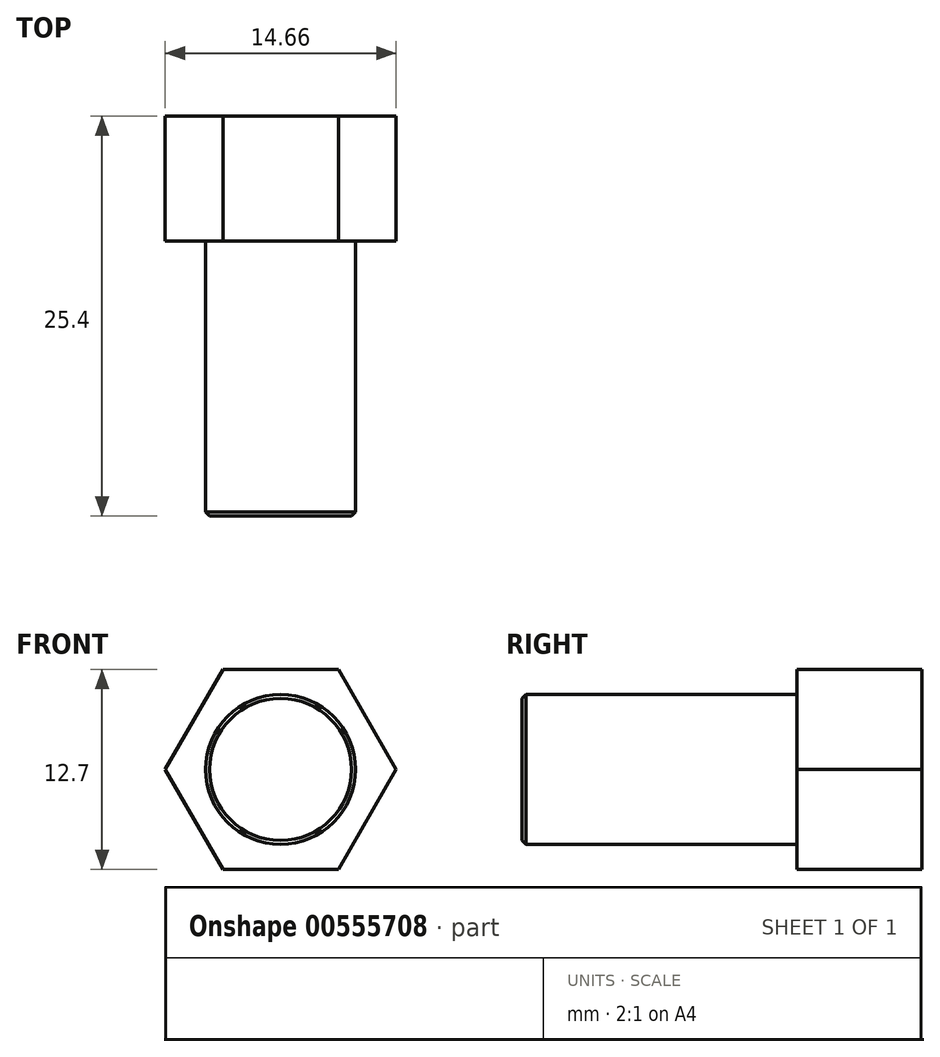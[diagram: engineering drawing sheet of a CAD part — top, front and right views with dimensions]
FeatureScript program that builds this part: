
annotation { "Feature Type Name" : "Feature", "Feature Type Description" : "" }
export const myFeature = defineFeature(function(context is Context, id is Id, definition is map)
    precondition{}
    {
        {
            var Q0;
            Q0=qCreatedBy(makeId("Front.planeOp"),FACE);
            var sketch = newSketch(context, id + "F0", { "sketchPlane" : qUnion([Q0])});
            skCircle(sketch, "E0", {"center": v(0, 0) * mm, "radius": 4.76 * mm});
            skSolve(sketch);
        }
        {
            var Q0;
            Q0=makeQuery(id+"F0.imprint","IMPRINT",FACE,{"disambiguationData":[TD([[makeQuery(id+"F0.imprint","IMPRINT",EDGE,{"derivedFrom":sQuery(id+"F0.wireOp",EDGE,"E0")}),1.0]])]});
            extrude(context, id + "F1", {"entities" : qUnion([Q0]), "depth" : 25.4 * mm, "offsetDistance" : 25.4 * mm});
        }
        {
            var Q0;
            Q0=qCreatedBy(makeId("Front.planeOp"),FACE);
            var sketch = newSketch(context, id + "F2", { "sketchPlane" : qUnion([Q0])});
            skCircle(sketch, "E1", {"center": v(0, 0) * mm, "radius": 6.35 * mm});
            skLineSegment(sketch, "E2", {"start": v(-3.67, 6.35) * mm, "end": v(3.67, 6.35) * mm});
            skLineSegment(sketch, "E3", {"start": v(3.67, 6.35) * mm, "end": v(7.33, 0) * mm});
            skLineSegment(sketch, "E4", {"start": v(7.33, 0) * mm, "end": v(3.67, -6.35) * mm});
            skLineSegment(sketch, "E5", {"start": v(3.67, -6.35) * mm, "end": v(-3.67, -6.35) * mm});
            skLineSegment(sketch, "E6", {"start": v(-3.67, -6.35) * mm, "end": v(-7.33, 0) * mm});
            skLineSegment(sketch, "E7", {"start": v(-7.33, 0) * mm, "end": v(-3.67, 6.35) * mm});
            skSolve(sketch);
        }
        {
            var Q0;
            {var subQ0=sQuery(id+"F2.wireOp",EDGE,"E2");var subQ1=sQuery(id+"F2.wireOp",EDGE,"E1");var subQ2=makeQuery(id+"F2.imprint","INTERSECT",VERTEX,{"derivedFrom":[subQ1,subQ0]});Q0=makeQuery(id+"F2.imprint","IMPRINT",FACE,{"disambiguationData":[TD([[makeQuery(id+"F2.imprint","IMPRINT",EDGE,{"disambiguationData":[TD([[subQ2,-1.0]])],"derivedFrom":subQ1}),-1.0]])]});}
            var Q1;
            {var subQ0=sQuery(id+"F2.wireOp",EDGE,"E7");var subQ1=sQuery(id+"F2.wireOp",EDGE,"E1");var subQ2=makeQuery(id+"F2.imprint","INTERSECT",VERTEX,{"derivedFrom":[subQ1,subQ0]});Q1=makeQuery(id+"F2.imprint","IMPRINT",FACE,{"disambiguationData":[TD([[makeQuery(id+"F2.imprint","IMPRINT",EDGE,{"disambiguationData":[TD([[subQ2,-1.0]])],"derivedFrom":subQ1}),-1.0]])]});}
            var Q2;
            {var subQ0=sQuery(id+"F2.wireOp",EDGE,"E6");var subQ1=sQuery(id+"F2.wireOp",EDGE,"E1");var subQ2=makeQuery(id+"F2.imprint","INTERSECT",VERTEX,{"derivedFrom":[subQ1,subQ0]});Q2=makeQuery(id+"F2.imprint","IMPRINT",FACE,{"disambiguationData":[TD([[makeQuery(id+"F2.imprint","IMPRINT",EDGE,{"disambiguationData":[TD([[subQ2,-1.0]])],"derivedFrom":subQ1}),-1.0]])]});}
            var Q3;
            {var subQ0=sQuery(id+"F2.wireOp",EDGE,"E2");var subQ1=sQuery(id+"F2.wireOp",EDGE,"E1");var subQ2=makeQuery(id+"F2.imprint","INTERSECT",VERTEX,{"derivedFrom":[subQ1,subQ0]});Q3=makeQuery(id+"F2.imprint","IMPRINT",FACE,{"disambiguationData":[TD([[makeQuery(id+"F2.imprint","IMPRINT",EDGE,{"disambiguationData":[TD([[subQ2,1.0]])],"derivedFrom":subQ1}),-1.0]])]});}
            var Q4;
            {var subQ0=sQuery(id+"F2.wireOp",EDGE,"E3");var subQ1=sQuery(id+"F2.wireOp",EDGE,"E1");var subQ2=makeQuery(id+"F2.imprint","INTERSECT",VERTEX,{"derivedFrom":[subQ1,subQ0]});Q4=makeQuery(id+"F2.imprint","IMPRINT",FACE,{"disambiguationData":[TD([[makeQuery(id+"F2.imprint","IMPRINT",EDGE,{"disambiguationData":[TD([[subQ2,1.0]])],"derivedFrom":subQ1}),-1.0]])]});}
            var Q5;
            {var subQ0=sQuery(id+"F2.wireOp",EDGE,"E5");var subQ1=sQuery(id+"F2.wireOp",EDGE,"E1");var subQ2=makeQuery(id+"F2.imprint","INTERSECT",VERTEX,{"derivedFrom":[subQ1,subQ0]});Q5=makeQuery(id+"F2.imprint","IMPRINT",FACE,{"disambiguationData":[TD([[makeQuery(id+"F2.imprint","IMPRINT",EDGE,{"disambiguationData":[TD([[subQ2,-1.0]])],"derivedFrom":subQ1}),-1.0]])]});}
            var Q6;
            {var subQ0=sQuery(id+"F2.wireOp",EDGE,"E1");var subQ4=makeQuery(id+"F2.imprint","INTERSECT",VERTEX,{"derivedFrom":[subQ0,sQuery(id+"F2.wireOp",EDGE,"E2")]});Q6=makeQuery(id+"F2.imprint","IMPRINT",FACE,{"disambiguationData":[TD([[makeQuery(id+"F2.imprint","IMPRINT",EDGE,{"disambiguationData":[TD([[subQ4,1.0]])],"derivedFrom":subQ0}),1.0]])]});}
            extrude(context, id + "F3", {"entities" : qUnion([Q0, Q1, Q2, Q3, Q4, Q5, Q6]), "operationType" : NewBodyOperationType.ADD, "depth" : 7.94 * mm, "offsetDistance" : 25.4 * mm});
        }
        {
            var Q0;
            Q0=makeQuery(id+"F1.opExtrude","CAP_EDGE",EDGE,{"disambiguationData":[OSD([sQuery(id+"F0.wireOp",EDGE,"E0")])],"isStart":false});
            chamfer(context, id + "F4", {"entities" : qUnion([Q0]), "width" : 0.25 * mm, "tangentPropagation" : true});
        }
    });
